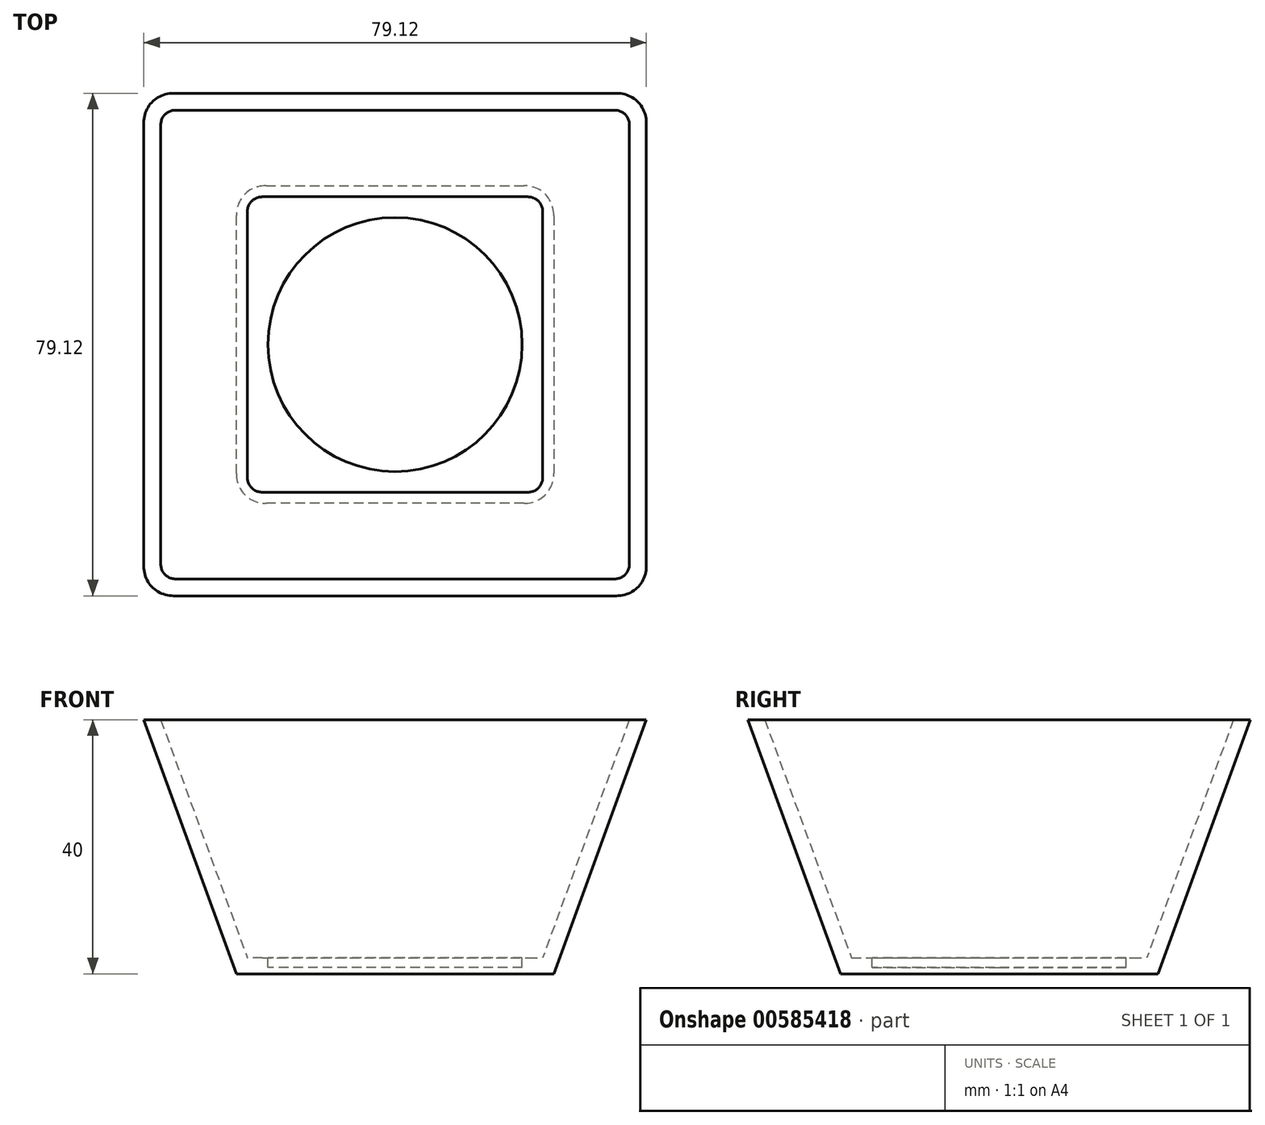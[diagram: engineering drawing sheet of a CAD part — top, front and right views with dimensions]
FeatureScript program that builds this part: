
annotation { "Feature Type Name" : "Feature", "Feature Type Description" : "" }
export const myFeature = defineFeature(function(context is Context, id is Id, definition is map)
    precondition{}
    {
        {
            var Q0;
            Q0=qCreatedBy(makeId("Top.planeOp"),FACE);
            var sketch = newSketch(context, id + "F0", { "sketchPlane" : qUnion([Q0])});
            skLineSegment(sketch, "E0.bottom", {"start": v(-25, 25) * mm, "end": v(25, 25) * mm});
            skLineSegment(sketch, "E0.top", {"start": v(-25, -25) * mm, "end": v(25, -25) * mm});
            skLineSegment(sketch, "E0.left", {"start": v(-25, 25) * mm, "end": v(-25, -25) * mm});
            skLineSegment(sketch, "E0.right", {"start": v(25, 25) * mm, "end": v(25, -25) * mm});
            skSolve(sketch);
        }
        {
            var Q0;
            Q0=makeQuery(id+"F0.imprint","IMPRINT",FACE,{"disambiguationData":[TD([[makeQuery(id+"F0.imprint","IMPRINT",EDGE,{"derivedFrom":sQuery(id+"F0.wireOp",EDGE,"E0.bottom")}),-1.0]])]});
            extrude(context, id + "F1", {"entities" : qUnion([Q0]), "depth" : 40 * mm, "offsetDistance" : 25 * mm, "hasDraft" : true, "draftAngle" : 20 * degree});
        }
        {
            var Q0;
            Q0=makeQuery(id+"F1.opExtrude","SWEPT_EDGE",EDGE,{"disambiguationData":[OSD([sQuery(id+"F0.wireOp",EDGE,"E0.bottom"),sQuery(id+"F0.wireOp",EDGE,"E0.right")])]});
            var Q1;
            Q1=makeQuery(id+"F1.opExtrude","SWEPT_EDGE",EDGE,{"disambiguationData":[OSD([sQuery(id+"F0.wireOp",EDGE,"E0.bottom"),sQuery(id+"F0.wireOp",EDGE,"E0.left")])]});
            var Q2;
            Q2=makeQuery(id+"F1.opExtrude","SWEPT_EDGE",EDGE,{"disambiguationData":[OSD([sQuery(id+"F0.wireOp",EDGE,"E0.top"),sQuery(id+"F0.wireOp",EDGE,"E0.right")])]});
            var Q3;
            Q3=makeQuery(id+"F1.opExtrude","SWEPT_EDGE",EDGE,{"disambiguationData":[OSD([sQuery(id+"F0.wireOp",EDGE,"E0.top"),sQuery(id+"F0.wireOp",EDGE,"E0.left")])]});
            fillet(context, id + "F2", {"entities" : qUnion([Q0, Q1, Q2, Q3]), "radius" : 5 * mm, "tangentPropagation" : true, "allowEdgeOverflow" : false});
        }
        {
            var Q0;
            Q0=makeQuery(id+"F1.opExtrude","CAP_FACE",FACE,{"disambiguationData":[OSD([sQuery(id+"F0.wireOp",EDGE,"E0.bottom"),sQuery(id+"F0.wireOp",EDGE,"E0.top"),sQuery(id+"F0.wireOp",EDGE,"E0.left"),sQuery(id+"F0.wireOp",EDGE,"E0.right")])],"isStart":false});
            shell(context, id + "F3", {"entities" : qUnion([Q0]), "thickness" : 2.5 * mm});
        }
        {
            var Q0;
            Q0=makeQuery(id+"F3.opShell","OFFSET_FACE",FACE,{"disambiguationData":[OSD([sQuery(id+"F0.wireOp",EDGE,"E0.bottom"),sQuery(id+"F0.wireOp",EDGE,"E0.top"),sQuery(id+"F0.wireOp",EDGE,"E0.left"),sQuery(id+"F0.wireOp",EDGE,"E0.right")])]});
            var sketch = newSketch(context, id + "F4", { "sketchPlane" : qUnion([Q0])});
            skCircle(sketch, "E1", {"center": v(0, 0) * mm, "radius": 20 * mm});
            skSolve(sketch);
        }
        {
            var Q0;
            Q0=makeQuery(id+"F4.imprint","IMPRINT",FACE,{"disambiguationData":[TD([[makeQuery(id+"F4.imprint","IMPRINT",EDGE,{"derivedFrom":sQuery(id+"F4.wireOp",EDGE,"E1")}),1.0]])]});
            extrude(context, id + "F5", {"entities" : qUnion([Q0]), "operationType" : NewBodyOperationType.REMOVE, "oppositeDirection" : true, "depth" : 1.5 * mm, "offsetDistance" : 25 * mm});
        }
    });
